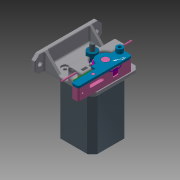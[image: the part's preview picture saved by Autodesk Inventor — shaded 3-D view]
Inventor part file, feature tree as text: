
AUTODESK INVENTOR PART (.ipt)
format: ipt  version: 2014 (Build 180170000, 170)  size: 976,384 bytes
history: native  units: mm
features: extrude x39, sketch x36, other x22, projected_geometry x22, hole x6, chamfer x4, fillet x4, plane x2, split x2, boolean_combine x1, loft x1
ambient origin geometry x8: Origin, YZ Plane, XZ Plane, XY Plane, X Axis, Y Axis, Z Axis, Center Point
bodies: Solid8 (feature_tree), Solid10 (feature_tree)
feature tree (139):
  extrude  "extruder base"  Depth=54.3mm
  other  "mtb skh"
  extrude  "mounting plate base"  TaperAngle=0.0deg  [1 undecoded]
  hole  "motor mount holes"  [1 undecoded]
  other  "moto mount screw holes"
  other  "motor mount screw cutout"
  hole  "motor mount hole counterbore"  [1 undecoded]
  hole  "mount base cutout"  [1 undecoded]
  extrude  "Extrusion2"  Depth=1.0mm
  chamfer  "motor side cham"  Distance=1.0mm
  chamfer  "motor rear cham"  Distance=80.0mm
  extrude  "motor_thingy"  Depth=76.3mm
  extrude  "motor shaft"  TaperAngle=0.0deg  [1 undecoded]
  extrude  "motor_shaft_d"  Depth=8.0mm
  other  "filament plane"
  extrude  "drive_gear"  TaperAngle=0.0deg  [1 undecoded]
  other  "hobb"
  other  "filament_center_point"
  other  "filament axis"
  extrude  "filament ex"  Depth=6.675mm
  extrude  "mounting plate"  TaperAngle=0.0deg  [1 undecoded]
  extrude  "Extrusion9"  Depth=0.75mm
  sketch  "Sketch15"  dims[d39=27.0mm]
  plane  "Work Plane3"
  extrude  "Extrusion10"  TaperAngle=0.0deg  [1 undecoded]
  extrude  "Extrusion11"  Depth=7.0mm
  extrude  "Extrusion12"  Depth=9.35mm
  extrude  "Extrusion13"  TaperAngle=0.0deg  [1 undecoded]
  sketch  "Sketch19"  dims[d43=0.0mm]
  extrude  "Extrusion14"  Depth=2.0mm
  extrude  "Extrusion44"  Depth=0.5mm
  fillet  "Fillet1"  Radius=6.2mm
  other  "tensioner nut skh"
  extrude  "tensioner nut ext"  Depth=2.0mm
  other  "nut slot pln"
  extrude  "tensioner nut slot"  Depth=2.0mm
  hole  "tension nut hole 1"  [1 undecoded]
  extrude  "tension nut hole"  Depth=2.5mm
  extrude  "lower filament guide"  Depth=1.0mm TaperAngle=0.0deg
  extrude  "tensioner base"  [1 undecoded]
  extrude  "tensioner bearing cutout"  Depth=1.0mm TaperAngle=0.0deg
  extrude  "tensioner top hole"  Depth=2.0mm TaperAngle=0.0deg
  other  "cap_screw_pln"
  extrude  "Extrusion22"  Depth=2.0mm
  extrude  "Extrusion23"  Depth=2.0mm
  sketch  "Sketch32"  dims[d51=3.875mm]
  plane  "Work Plane6"
  extrude  "Extrusion30"  Depth=1.0mm
  extrude  "Extrusion45"  Depth=2.0mm
  fillet  "Fillet7"  Radius=2.0mm
  split  "Split1"
  split  "Split2"
  boolean_combine  "Combine1"
  extrude  "Extrusion24"  Depth=2.0mm TaperAngle=0.0deg
  extrude  "Extrusion25"  Depth=2.0mm
  extrude  "tensioner assembly clearance"  Depth=0.25mm
  hole  "mountin gholes"  [1 undecoded]
  extrude  "gusset 1"  Depth=0.75mm TaperAngle=0.0deg
  extrude  "gusset 2"  Depth=7.25mm
  chamfer  "Chamfer4"  [1 undecoded]
  fillet  "Fillet4"  Radius=24.2mm
  chamfer  "Chamfer3"  Distance=7.25mm
  fillet  "Fillet5"  [1 undecoded]
  extrude  "Extrusion31"  Depth=6.0mm
  extrude  "Extrusion32"  Depth=7.25mm
  extrude  "Extrusion40"  TaperAngle=0.0deg  [1 undecoded]
  extrude  "Extrusion41"  TaperAngle=0.0deg  [1 undecoded]
  extrude  "Extrusion42"  Depth=2.0mm TaperAngle=0.0deg
  extrude  "Extrusion43"  Depth=2.0mm
  hole  "Hole7"  [1 undecoded]
  sketch  "Sketch61"  dims[d81=7.0mm d82=0.0mm]
  sketch  "Sketch62"  dims[d83=8.0mm d84=100.0mm d85=0.0mm d86=0.0mm d87=2.0mm d88=0.5mm d95=6.2mm d96=3.0mm d97=5.0mm d98=3.0mm d99=2.5mm d100=1.0mm d101=0.0mm d102=-3.25mm d103=1.0mm d104=0.0mm d105=3.6mm d106=6.0mm d107=8.4mm d108=2.3mm d109=14.3117mm d110=8.0mm d111=20.594885mm d112=2.0mm d113=0.0mm d114=8.0mm d115=20.0mm d116=-1.745329mm d117=1.0mm d118=8.0mm d119=2.0mm d122=20.0mm d123=0.0mm d124=0.6mm d125=0.25mm d126=7.75mm d127=0.75mm d128=0.0mm d129=0.0mm d130=7.25mm d131=0.0mm d132=24.2mm d133=7.25mm d134=0.0mm d135=6.0mm d136=7.25mm d137=0.0mm d138=0.0mm d139=20.0mm d140=0.0mm d143=3.5mm d144=4.0mm d145=20.0mm d146=0.0mm d148=20.0mm d149=0.0mm d151=20.0mm d152=0.0mm d153=6.0mm d154=4.915mm d155=6.0mm d156=8.433mm d157=2.3mm d158=14.3117mm d159=8.0mm d160=20.594885mm d162=45.0deg d163=3.0mm d164=0.0mm d165=3.0mm d166=0.0mm d167=2.0mm d168=6.0mm d169=1.0mm d170=1.0mm d171=2.0mm d172=45.0deg d173=4.0mm d177=1.5mm d178=0.5mm d179=0.0mm d180=0.5mm d181=0.0mm d184=0.5mm d185=0.0mm d231=2.0mm d232=1.0mm d233=1.5mm d234=20.0mm d235=2.0mm d236=12.0mm d237=2.0mm d238=0.0mm d239=10.0mm d240=0.0mm d241=1.0mm d242=7.0mm d243=5.0mm d244=0.0mm d245=4.0mm d246=5.0mm d247=0.0mm d248=10.0mm d249=0.0mm d251=0.25mm d252=0.25mm d253=1.5mm d254=15.0mm d255=0.0mm d256=2.0mm d257=3.0mm d258=2.0mm d259=6.0mm d260=4.0mm d261=2.0mm d262=90.0deg d263=8.0mm d264=20.594885mm d265=5.0mm d266=2.0mm d267=45.0deg d270=3.5mm d271=0.0mm d272=90.0deg d273=0.0mm d274=90.0deg]
  loft  "Loft2"
  projected_geometry  "Projected Loop1"
  sketch  "Sketch3"  dims[d0=31.0mm d1=54.3mm]
  other  "motor"
  sketch  "Sketch4"  dims[d2=4.0mm d3=0.0mm]
  sketch  "Sketch5"  dims[d4=3.6mm d5=6.0mm d6=8.4mm d7=2.3mm d8=14.3117mm d9=8.0mm d10=20.594885mm]
  sketch  "Sketch6"  dims[d11=-2.0mm d12=8.4mm d13=6.0mm d14=8.4mm d15=2.3mm d16=14.3117mm d17=8.0mm d18=0.0mm d19=22.5mm]
  projected_geometry  "Projected Loop2"
  sketch  "Sketch7"  dims[d20=6.0mm d21=8.4mm d22=2.3mm d23=14.3117mm d24=8.0mm d25=20.594885mm d26=42.3mm]
  other  "drive gear"
  sketch  "Sketch8"  dims[d27=65.0mm d28=0.0mm d29=6.0mm d30=2.0mm d31=45.0deg]
  projected_geometry  "Projected Loop3"
  other  "filament"
  sketch  "Sketch12"  dims[d32=2.0mm d33=2.0mm d34=45.0deg d35=22.0mm d36=1.0mm d37=-3.490659mm]
  projected_geometry  "Projected Loop4"
  sketch  "Sketch14"  dims[d38=5.0mm]
  other  "bearing"
  projected_geometry  "Projected Loop7"
  projected_geometry  "Projected Loop8"
  sketch  "Sketch16"  dims[d40=0.0mm]
  sketch  "Sketch17"  dims[d41=1.25mm]
  sketch  "Sketch18"  dims[d42=27.0mm]
  projected_geometry  "Projected Loop10"
  other  "tensioner bolt skh"
  sketch  "Sketch24"  dims[d44=8.675mm]
  sketch  "Sketch25"  dims[d45=5.0mm]
  sketch  "Sketch26"  dims[d46=11.0mm]
  projected_geometry  "Projected Loop11"
  other  "tensioner"
  sketch  "Sketch27"  dims[d47=8.3mm]
  sketch  "Sketch28"  dims[d48=0.0mm]
  sketch  "Sketch29"  dims[d49=4.7mm]
  sketch  "Sketch30"  dims[d50=0.0mm]
  other  "Srf1"
  projected_geometry  "Projected Loop13"
  sketch  "Sketch35"  dims[d52=90.0deg]
  sketch  "Sketch36"  dims[d56=0.875mm]
  projected_geometry  "Projected Loop14"
  sketch  "Sketch37"  dims[d57=1.75mm d58=80.0mm d59=0.0mm]
  projected_geometry  "Projected Loop15"
  projected_geometry  "Projected Loop16"
  sketch  "Sketch38"  dims[d60=20.0mm d61=76.3mm]
  projected_geometry  "Projected Loop17"
  sketch  "Sketch41"  dims[d62=4.0mm d63=0.0mm]
  sketch  "Sketch42"  dims[d64=22.0mm d65=8.0mm]
  other  "tensioner washer"
  sketch  "Sketch43"  dims[d66=7.0mm d67=0.0mm]
  other  "wedge"
  sketch  "Sketch54"  dims[d68=12.35mm d70=6.675mm]
  projected_geometry  "Projected Loop29"
  sketch  "Sketch55"  dims[d71=7.0mm d72=0.0mm]
  projected_geometry  "Projected Loop30"
  sketch  "Sketch56"  dims[d73=2.0mm d74=0.75mm]
  projected_geometry  "Projected Loop31"
  sketch  "Sketch57"  dims[d75=7.0mm d76=0.0mm]
  projected_geometry  "Projected Loop32"
  projected_geometry  "Projected Loop33"
  sketch  "Sketch58"  dims[d77=0.5mm d78=7.0mm]
  projected_geometry  "Projected Loop34"
  sketch  "Sketch59"  dims[d79=0.0mm d80=9.35mm]
  projected_geometry  "Projected Loop35"
  other  "Edges1"
  extrude  "ExtrusionSrf1"  Depth=2.0mm TaperAngle=0.0deg
  projected_geometry  "Project Cut Edges2"
  other  "tensioner bottom"
  other  "tensioner top"
  projected_geometry  "Project Cut Edges4"
note: 17 required parameter values undecoded (feature->parameter linkage not recoverable at this tier; creation-order binding heuristic only, values carry confidence <= 0.55)
